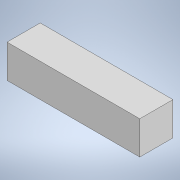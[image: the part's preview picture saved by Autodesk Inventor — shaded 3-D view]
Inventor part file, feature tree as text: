
AUTODESK INVENTOR PART (.ipt)
format: ipt  version: 2021 (Build 250183000, 183)  size: 87,040 bytes
history: native  units: mm
features: extrude x1, sketch x1
ambient origin geometry x8: Origin, YZ Plane, XZ Plane, XY Plane, X Axis, Y Axis, Z Axis, Center Point
bodies: Solid1 (feature_tree)
feature tree (2):
  extrude  "Extrusion1"  Depth=5.0mm
  sketch  "Sketch1"  dims[d0=5.0mm d1=5.0mm d2=20.0mm d3=0.0mm]
